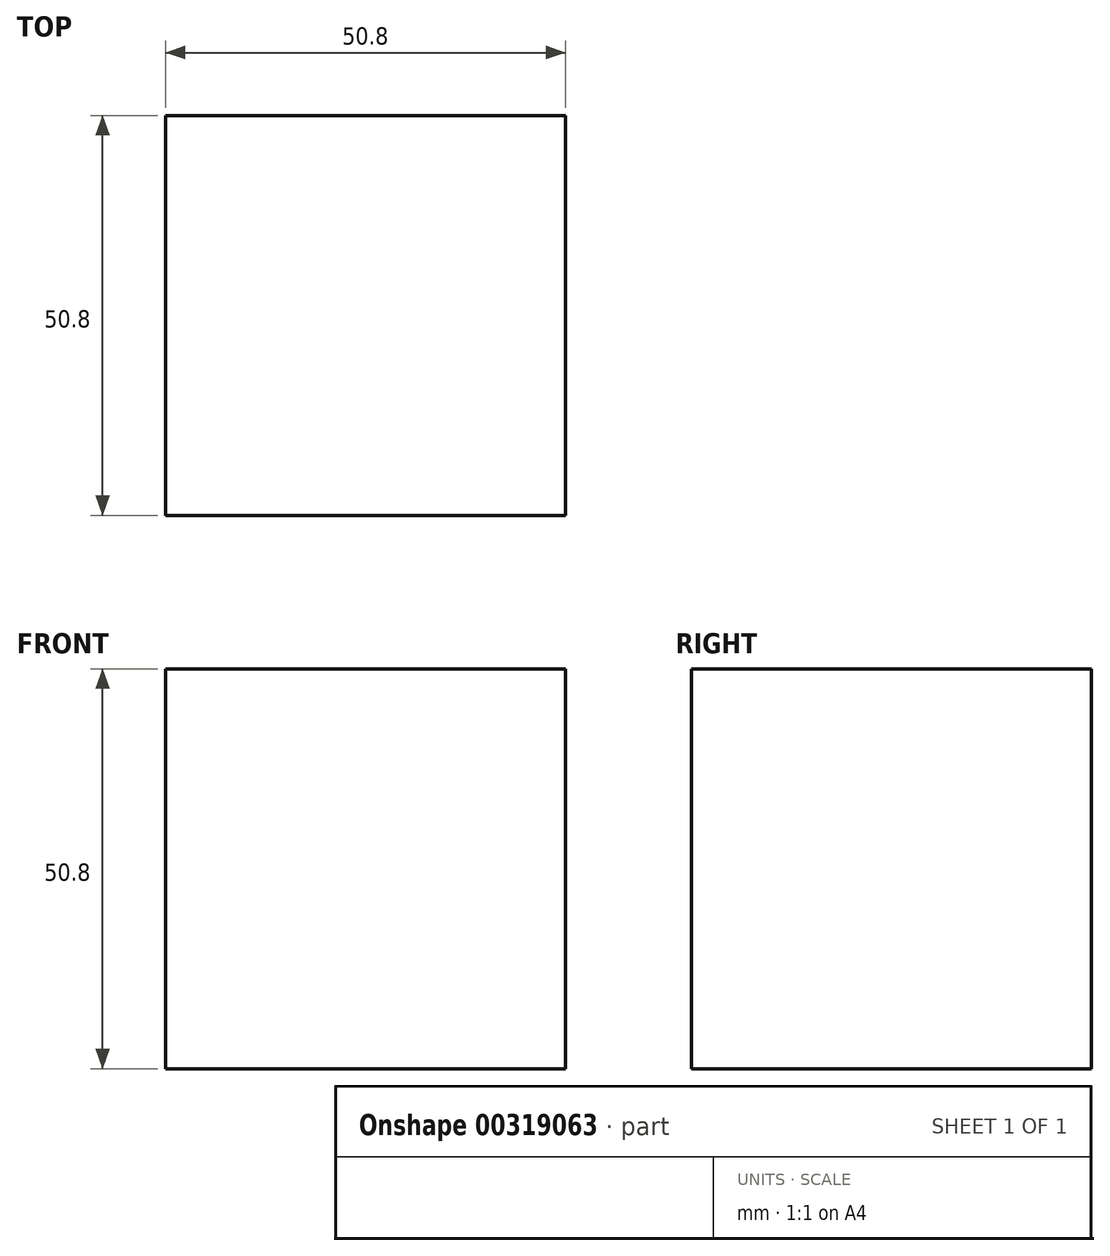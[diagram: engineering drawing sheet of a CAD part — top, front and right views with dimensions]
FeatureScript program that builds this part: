
annotation { "Feature Type Name" : "Feature", "Feature Type Description" : "" }
export const myFeature = defineFeature(function(context is Context, id is Id, definition is map)
    precondition{}
    {
        {
            var Q0;
            Q0=qCreatedBy(makeId("Front.planeOp"),FACE);
            var sketch = newSketch(context, id + "F0", { "sketchPlane" : qUnion([Q0])});
            skPoint(sketch, "E0.middle", {"position": v(0, 0) * mm});
            skLineSegment(sketch, "E1.bottom", {"start": v(25.4, -25.4) * mm, "end": v(-25.4, -25.4) * mm});
            skLineSegment(sketch, "E1.top", {"start": v(25.4, 25.4) * mm, "end": v(-25.4, 25.4) * mm});
            skLineSegment(sketch, "E1.left", {"start": v(25.4, -25.4) * mm, "end": v(25.4, 25.4) * mm});
            skLineSegment(sketch, "E1.right", {"start": v(-25.4, -25.4) * mm, "end": v(-25.4, 25.4) * mm});
            skSolve(sketch);
        }
        {
            var Q0;
            Q0 = qSketchRegion(id + "F0", true);
            extrude(context, id + "F1", {"entities" : qUnion([Q0]), "depth" : 50.8 * mm});
        }
    });
